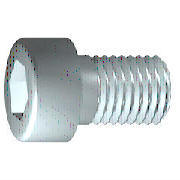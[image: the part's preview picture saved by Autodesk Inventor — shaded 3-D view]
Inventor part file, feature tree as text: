
AUTODESK INVENTOR PART (.ipt)
format: ipt  version: 2025.2 (Build 292293000, 293)  size: 201,728 bytes
history: native  units: mm (DEFAULTED — no unit token found)
features: other x1, extrude x1, chamfer x1, plane x1, fillet x1
ambient origin geometry x7: Origin, YZ Plane, XY Plane, X Axis, Y Axis, Z Axis, Center Point
bodies: Solid1 (feature_tree)
feature tree (5):
  other  "Körper"
  extrude  "Loch"  Depth=1.8mm
  chamfer  "Fase1"  Distance=0.24548mm
  plane  "Work Plane1"
  fillet  "Fillet2"  Radius=2.0mm
